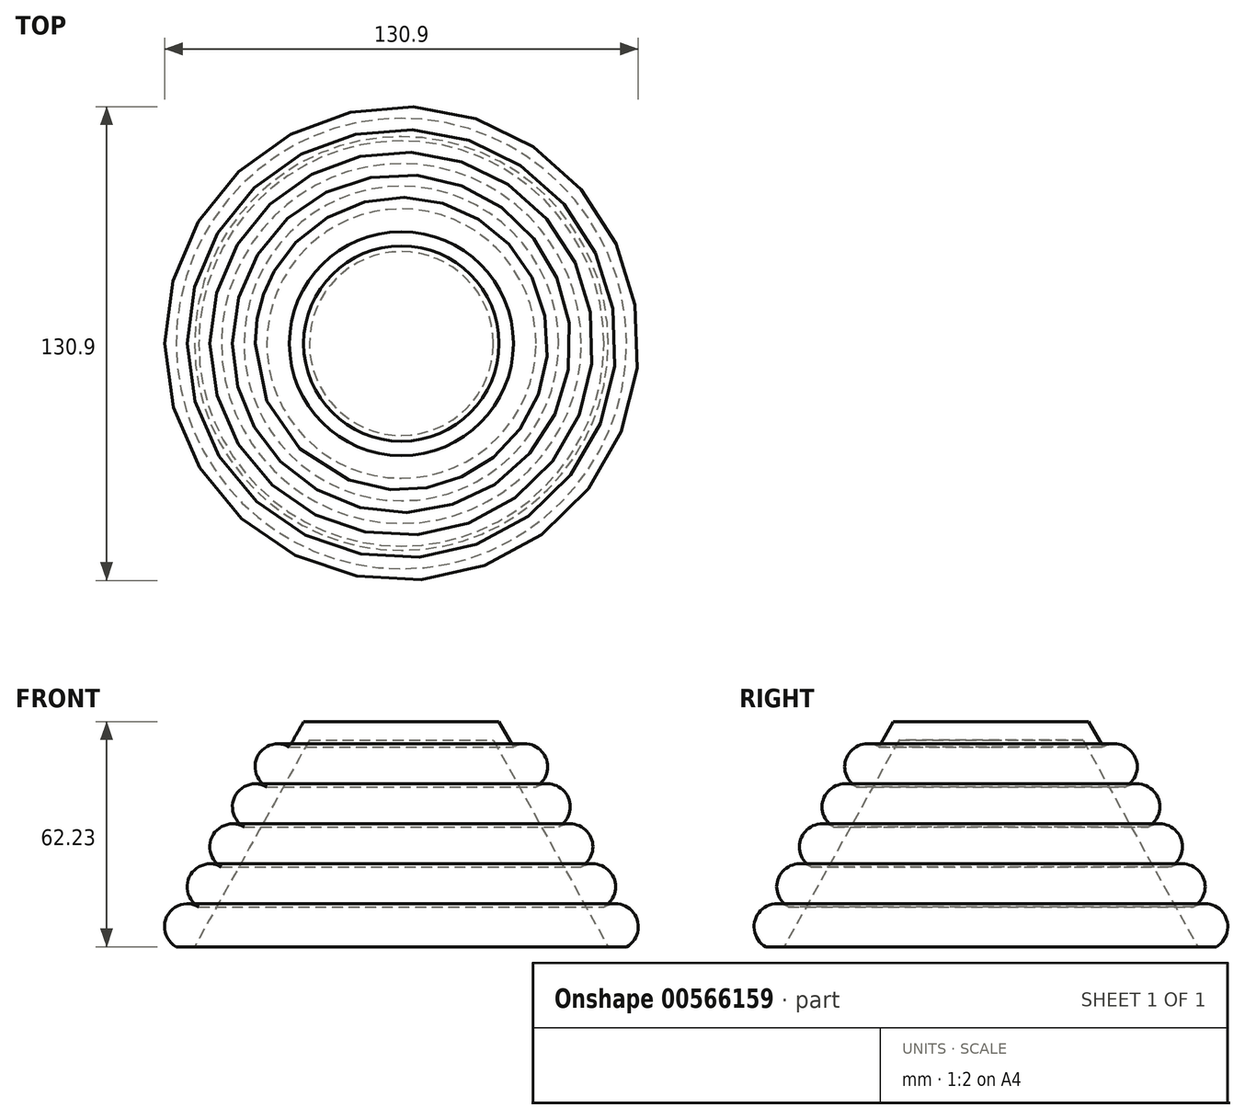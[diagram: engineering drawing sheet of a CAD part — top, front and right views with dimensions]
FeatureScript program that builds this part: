
annotation { "Feature Type Name" : "Feature", "Feature Type Description" : "" }
export const myFeature = defineFeature(function(context is Context, id is Id, definition is map)
    precondition{}
    {
        {
            var Q0;
            Q0=qCreatedBy(makeId("Right.planeOp"),FACE);
            var sketch = newSketch(context, id + "F0", { "sketchPlane" : qUnion([Q0])});
            skLineSegment(sketch, "E0", {"start": v(0, 0) * mm, "end": v(0, 57.15) * mm, "construction": true});
            skLineSegment(sketch, "E1", {"start": v(0, 57.15) * mm, "end": v(0, 62.23) * mm});
            skLineSegment(sketch, "E2", {"start": v(0, 62.23) * mm, "end": v(-26.99, 62.23) * mm});
            skLineSegment(sketch, "E3", {"start": v(-26.99, 62.23) * mm, "end": v(-62.23, 0) * mm, "construction": true});
            skLineSegment(sketch, "E4", {"start": v(-62.23, 0) * mm, "end": v(-57.15, 0) * mm});
            skLineSegment(sketch, "E5", {"start": v(-57.15, 0) * mm, "end": v(-25.4, 57.15) * mm});
            skLineSegment(sketch, "E6", {"start": v(-25.4, 57.15) * mm, "end": v(0, 57.15) * mm});
            skArc(sketch, "E7.trimOffspring", {"start": v(-55.97, 11.05) * mm, "mid": v(-64.63, 8.65) * mm, "end": v(-62.23, 0) * mm});
            skArc(sketch, "E8.trimOffspring", {"start": v(-49.72, 22.1) * mm, "mid": v(-58.37, 19.7) * mm, "end": v(-55.97, 11.05) * mm});
            skArc(sketch, "E9.trimOffspring", {"start": v(-43.46, 33.15) * mm, "mid": v(-52.11, 30.76) * mm, "end": v(-49.72, 22.1) * mm});
            skArc(sketch, "E10.trimOffspring", {"start": v(-37.2, 44.2) * mm, "mid": v(-45.85, 41.8) * mm, "end": v(-43.46, 33.15) * mm});
            skArc(sketch, "E11.trimOffspring", {"start": v(-30.94, 55.25) * mm, "mid": v(-39.6, 52.86) * mm, "end": v(-37.2, 44.2) * mm});
            skLineSegment(sketch, "E12", {"start": v(-30.94, 55.25) * mm, "end": v(-26.99, 62.23) * mm});
            skSolve(sketch);
        }
        {
            var Q0;
            Q0 = qSketchRegion(id + "F0", true);
            var Q1;
            Q1=sQuery(id+"F0.wireOp",EDGE,"E0");
            revolve(context, id + "F1", {"entities" : qUnion([Q0]), "axis" : qUnion([Q1]), "revolveType" : RevolveType.FULL});
        }
    });
